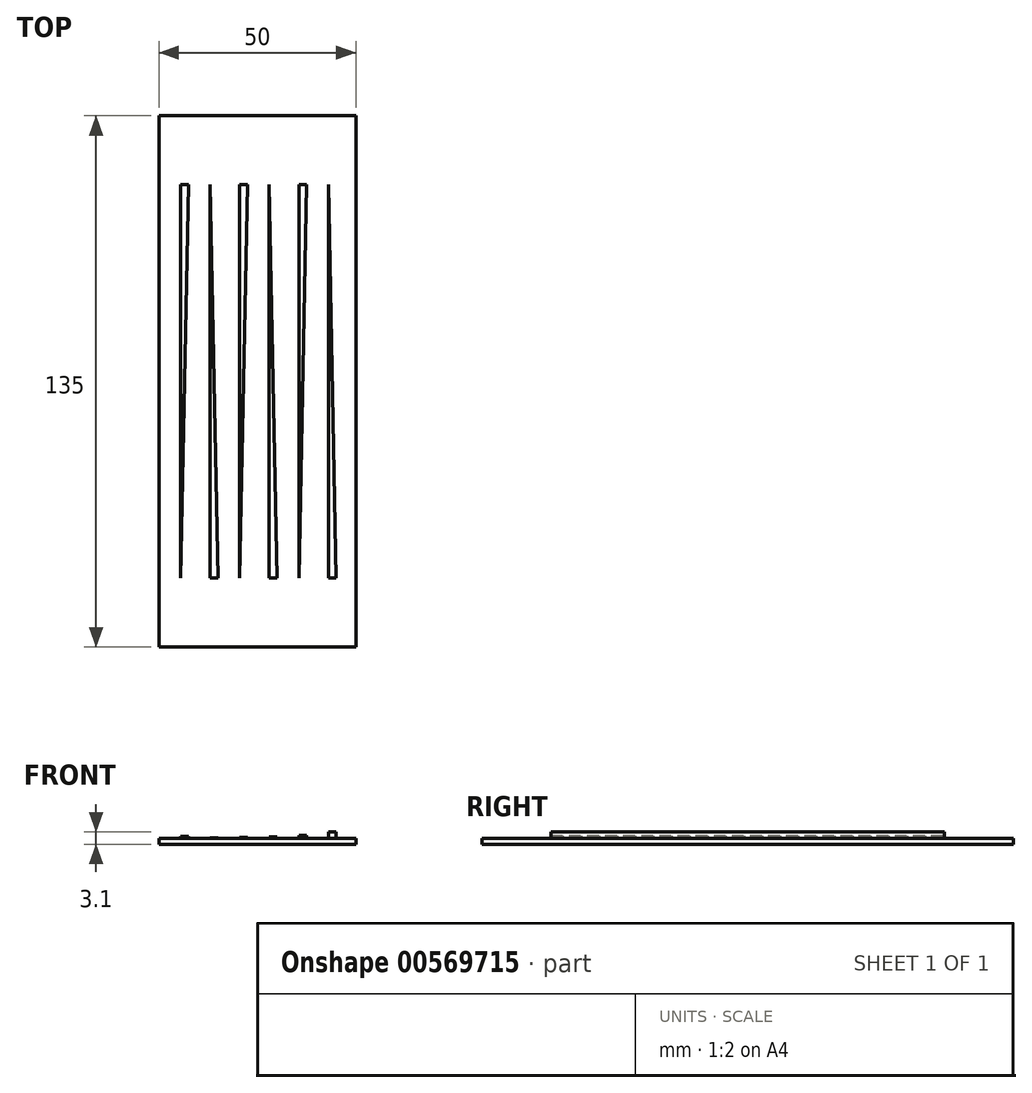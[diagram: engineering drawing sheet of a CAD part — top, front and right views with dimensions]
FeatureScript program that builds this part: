
annotation { "Feature Type Name" : "Feature", "Feature Type Description" : "" }
export const myFeature = defineFeature(function(context is Context, id is Id, definition is map)
    precondition{}
    {
        {
            var Q0;
            Q0=qCreatedBy(makeId("Top.planeOp"),FACE);
            var sketch = newSketch(context, id + "F0", { "sketchPlane" : qUnion([Q0])});
            skLineSegment(sketch, "E0", {"start": v(0, 0) * mm, "end": v(0, 100) * mm});
            skLineSegment(sketch, "E1", {"start": v(0, 100) * mm, "end": v(2, 100) * mm});
            skLineSegment(sketch, "E2", {"start": v(2, 100) * mm, "end": v(0, 0) * mm});
            skLineSegment(sketch, "E3.1.0.0", {"start": v(7.5, 0) * mm, "end": v(7.5, 100) * mm});
            skLineSegment(sketch, "E3.1.0.1", {"start": v(7.5, 100) * mm, "end": v(9.5, 100) * mm});
            skLineSegment(sketch, "E3.1.0.2", {"start": v(9.5, 100) * mm, "end": v(7.5, 0) * mm});
            skLineSegment(sketch, "E3.2.0.0", {"start": v(15, 0) * mm, "end": v(15, 100) * mm});
            skLineSegment(sketch, "E3.2.0.1", {"start": v(15, 100) * mm, "end": v(17, 100) * mm});
            skLineSegment(sketch, "E3.2.0.2", {"start": v(17, 100) * mm, "end": v(15, 0) * mm});
            skLineSegment(sketch, "E3.3.0.0", {"start": v(22.5, 0) * mm, "end": v(22.5, 100) * mm});
            skLineSegment(sketch, "E3.3.0.1", {"start": v(22.5, 100) * mm, "end": v(24.5, 100) * mm});
            skLineSegment(sketch, "E3.3.0.2", {"start": v(24.5, 100) * mm, "end": v(22.5, 0) * mm});
            skLineSegment(sketch, "E3.4.0.0", {"start": v(30, 0) * mm, "end": v(30, 100) * mm});
            skLineSegment(sketch, "E3.4.0.1", {"start": v(30, 100) * mm, "end": v(32, 100) * mm});
            skLineSegment(sketch, "E3.4.0.2", {"start": v(32, 100) * mm, "end": v(30, 0) * mm});
            skLineSegment(sketch, "E3.5.0.0", {"start": v(37.5, 0) * mm, "end": v(37.5, 100) * mm});
            skLineSegment(sketch, "E3.5.0.1", {"start": v(37.5, 100) * mm, "end": v(39.5, 100) * mm});
            skLineSegment(sketch, "E3.5.0.2", {"start": v(39.5, 100) * mm, "end": v(37.5, 0) * mm});
            skLineSegment(sketch, "E3.direction1", {"start": v(0, 0) * mm, "end": v(7.5, 0) * mm, "construction": true});
            skLineSegment(sketch, "E4.bottom", {"start": v(-5.5, 117.5) * mm, "end": v(44.5, 117.5) * mm});
            skLineSegment(sketch, "E4.top", {"start": v(-5.5, -17.5) * mm, "end": v(44.5, -17.5) * mm});
            skLineSegment(sketch, "E4.left", {"start": v(-5.5, 117.5) * mm, "end": v(-5.5, -17.5) * mm});
            skLineSegment(sketch, "E4.right", {"start": v(44.5, 117.5) * mm, "end": v(44.5, -17.5) * mm});
            skPoint(sketch, "E5", {"position": v(19.5, 117.5) * mm});
            skPoint(sketch, "E6", {"position": v(-5.5, 50) * mm});
            skPoint(sketch, "E7", {"position": v(0, 50) * mm});
            skLineSegment(sketch, "E8", {"start": v(-5.5, 50) * mm, "end": v(44.5, 50) * mm, "construction": true});
            skSolve(sketch);
        }
        {
            var Q0;
            Q0=makeQuery(id+"F0.imprint","IMPRINT",FACE,{"disambiguationData":[TD([[makeQuery(id+"F0.imprint","IMPRINT",EDGE,{"derivedFrom":sQuery(id+"F0.wireOp",EDGE,"E0")}),1.0]])]});
            var Q1;
            Q1=makeQuery(id+"F0.imprint","IMPRINT",FACE,{"disambiguationData":[TD([[makeQuery(id+"F0.imprint","IMPRINT",EDGE,{"derivedFrom":sQuery(id+"F0.wireOp",EDGE,"E3.5.0.0")}),-1.0]])]});
            var Q2;
            Q2=makeQuery(id+"F0.imprint","IMPRINT",FACE,{"disambiguationData":[TD([[makeQuery(id+"F0.imprint","IMPRINT",EDGE,{"derivedFrom":sQuery(id+"F0.wireOp",EDGE,"E0")}),-1.0]])]});
            var Q3;
            Q3=makeQuery(id+"F0.imprint","IMPRINT",FACE,{"disambiguationData":[TD([[makeQuery(id+"F0.imprint","IMPRINT",EDGE,{"derivedFrom":sQuery(id+"F0.wireOp",EDGE,"E3.4.0.0")}),-1.0]])]});
            var Q4;
            Q4=makeQuery(id+"F0.imprint","IMPRINT",FACE,{"disambiguationData":[TD([[makeQuery(id+"F0.imprint","IMPRINT",EDGE,{"derivedFrom":sQuery(id+"F0.wireOp",EDGE,"E3.3.0.0")}),-1.0]])]});
            var Q5;
            Q5=makeQuery(id+"F0.imprint","IMPRINT",FACE,{"disambiguationData":[TD([[makeQuery(id+"F0.imprint","IMPRINT",EDGE,{"derivedFrom":sQuery(id+"F0.wireOp",EDGE,"E3.2.0.0")}),-1.0]])]});
            var Q6;
            Q6=makeQuery(id+"F0.imprint","IMPRINT",FACE,{"disambiguationData":[TD([[makeQuery(id+"F0.imprint","IMPRINT",EDGE,{"derivedFrom":sQuery(id+"F0.wireOp",EDGE,"E3.1.0.0")}),-1.0]])]});
            extrude(context, id + "F1", {"entities" : qUnion([Q0, Q1, Q2, Q3, Q4, Q5, Q6]), "oppositeDirection" : true, "depth" : 1.5 * mm, "offsetDistance" : 25 * mm});
        }
        {
            var Q0;
            Q0=makeQuery(id+"F0.imprint","IMPRINT",FACE,{"disambiguationData":[TD([[makeQuery(id+"F0.imprint","IMPRINT",EDGE,{"derivedFrom":sQuery(id+"F0.wireOp",EDGE,"E0")}),-1.0]])]});
            extrude(context, id + "F2", {"entities" : qUnion([Q0]), "depth" : .5 * mm, "offsetDistance" : 25 * mm});
        }
        {
            var Q0;
            Q0=makeQuery(id+"F0.imprint","IMPRINT",FACE,{"disambiguationData":[TD([[makeQuery(id+"F0.imprint","IMPRINT",EDGE,{"derivedFrom":sQuery(id+"F0.wireOp",EDGE,"E3.1.0.0")}),-1.0]])]});
            extrude(context, id + "F3", {"entities" : qUnion([Q0]), "oppositeDirection" : true, "depth" : .1 * mm, "offsetDistance" : 25 * mm});
        }
        {
            var Q0;
            Q0=makeQuery(id+"F0.imprint","IMPRINT",FACE,{"disambiguationData":[TD([[makeQuery(id+"F0.imprint","IMPRINT",EDGE,{"derivedFrom":sQuery(id+"F0.wireOp",EDGE,"E3.2.0.0")}),-1.0]])]});
            extrude(context, id + "F4", {"entities" : qUnion([Q0]), "depth" : .2 * mm, "offsetDistance" : 25 * mm});
        }
        {
            var Q0;
            Q0=makeQuery(id+"F0.imprint","IMPRINT",FACE,{"disambiguationData":[TD([[makeQuery(id+"F0.imprint","IMPRINT",EDGE,{"derivedFrom":sQuery(id+"F0.wireOp",EDGE,"E3.3.0.0")}),-1.0]])]});
            extrude(context, id + "F5", {"entities" : qUnion([Q0]), "oppositeDirection" : true, "depth" : .4 * mm, "offsetDistance" : 25 * mm});
        }
        {
            var Q0;
            Q0=makeQuery(id+"F0.imprint","IMPRINT",FACE,{"disambiguationData":[TD([[makeQuery(id+"F0.imprint","IMPRINT",EDGE,{"derivedFrom":sQuery(id+"F0.wireOp",EDGE,"E3.4.0.0")}),-1.0]])]});
            extrude(context, id + "F6", {"entities" : qUnion([Q0]), "depth" : .8 * mm, "offsetDistance" : 25 * mm});
        }
        {
            var Q0;
            Q0=makeQuery(id+"F0.imprint","IMPRINT",FACE,{"disambiguationData":[TD([[makeQuery(id+"F0.imprint","IMPRINT",EDGE,{"derivedFrom":sQuery(id+"F0.wireOp",EDGE,"E3.5.0.0")}),-1.0]])]});
            extrude(context, id + "F7", {"entities" : qUnion([Q0]), "oppositeDirection" : true, "depth" : 1.6 * mm, "offsetDistance" : 25 * mm});
        }
        {
            var Q0;
            Q0=makeQuery(id+"F3.opExtrude","SWEPT_BODY",BODY,{"disambiguationData":[OSD([sQuery(id+"F0.wireOp",EDGE,"E3.1.0.0"),sQuery(id+"F0.wireOp",EDGE,"E3.1.0.1"),sQuery(id+"F0.wireOp",EDGE,"E3.1.0.2")])]});
            var Q1;
            Q1=makeQuery(id+"F5.opExtrude","SWEPT_BODY",BODY,{"disambiguationData":[OSD([sQuery(id+"F0.wireOp",EDGE,"E3.3.0.0"),sQuery(id+"F0.wireOp",EDGE,"E3.3.0.1"),sQuery(id+"F0.wireOp",EDGE,"E3.3.0.2")])]});
            var Q2;
            Q2=makeQuery(id+"F7.opExtrude","SWEPT_BODY",BODY,{"disambiguationData":[OSD([sQuery(id+"F0.wireOp",EDGE,"E3.5.0.0"),sQuery(id+"F0.wireOp",EDGE,"E3.5.0.1"),sQuery(id+"F0.wireOp",EDGE,"E3.5.0.2")])]});
            var Q3;
            Q3=sQuery(id+"F0.wireOp",EDGE,"E8");
            transform(context, id + "F8", {"entities" : qUnion([Q0, Q1, Q2]), "transformType" : TransformType.ROTATION, "transformAxis" : qUnion([Q3]), "angle" : 180 * degree, "makeCopy" : false});
        }
    });
